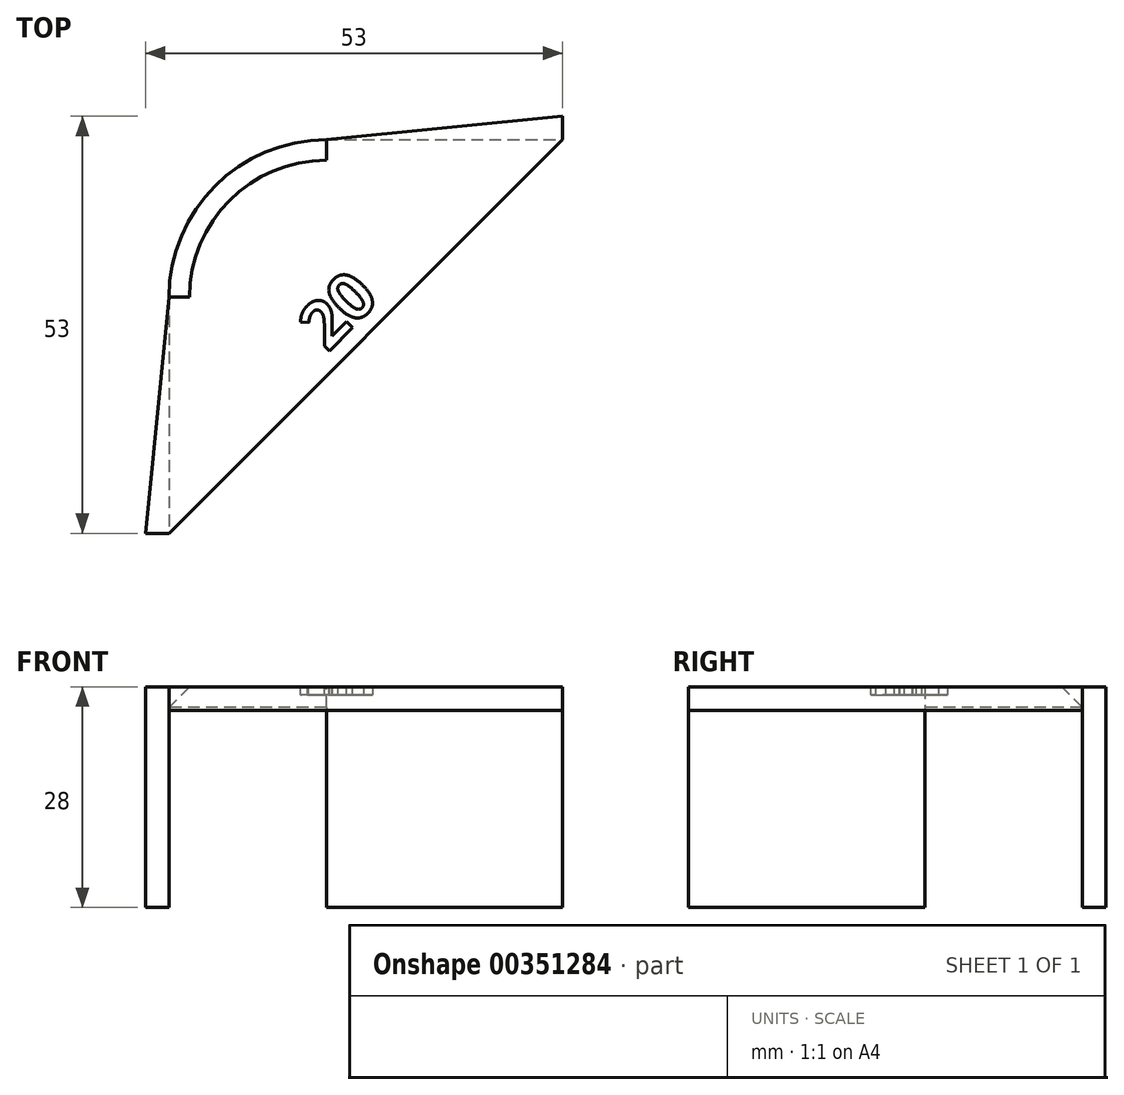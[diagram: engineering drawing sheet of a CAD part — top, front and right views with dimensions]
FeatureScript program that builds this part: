
annotation { "Feature Type Name" : "Feature", "Feature Type Description" : "" }
export const myFeature = defineFeature(function(context is Context, id is Id, definition is map)
    precondition{}
    {
        {
            var Q0;
            Q0=qCreatedBy(makeId("Top.planeOp"),FACE);
            var sketch = newSketch(context, id + "F0", { "sketchPlane" : qUnion([Q0])});
            skArc(sketch, "E0", {"start": v(0, 20) * mm, "mid": v(-14.14, 14.14) * mm, "end": v(-20, 0) * mm});
            skLineSegment(sketch, "E1", {"start": v(-20, 0) * mm, "end": v(-20, 20) * mm, "construction": true});
            skLineSegment(sketch, "E2", {"start": v(-20, 20) * mm, "end": v(0, 20) * mm, "construction": true});
            skPoint(sketch, "E3", {"position": v(0, 20) * mm});
            skPoint(sketch, "E4", {"position": v(-20, 0) * mm});
            skLineSegment(sketch, "E5", {"start": v(-20, 0) * mm, "end": v(-23, 0) * mm});
            skLineSegment(sketch, "E6", {"start": v(-23, -30) * mm, "end": v(-23, 0) * mm});
            skLineSegment(sketch, "E7", {"start": v(-23, -30) * mm, "end": v(-20, -30) * mm});
            skLineSegment(sketch, "E8", {"start": v(0, 20) * mm, "end": v(0, 23) * mm});
            skLineSegment(sketch, "E9", {"start": v(0, 23) * mm, "end": v(30, 23) * mm});
            skLineSegment(sketch, "E10", {"start": v(30, 23) * mm, "end": v(30, 20) * mm});
            skLineSegment(sketch, "E11", {"start": v(-20, -30) * mm, "end": v(30, 20) * mm});
            skPoint(sketch, "E12", {"position": v(-8.23, -18.23) * mm});
            skPoint(sketch, "E13", {"position": v(18.23, 8.23) * mm});
            skLineSegment(sketch, "E14", {"start": v(0, 20) * mm, "end": v(30, 20) * mm});
            skLineSegment(sketch, "E15", {"start": v(-20, 0) * mm, "end": v(-20, -30) * mm});
            skLineSegment(sketch, "E16", {"start": v(-20, -27.17) * mm, "end": v(27.17, 20) * mm, "construction": true});
            skPoint(sketch, "E17", {"position": v(3.59, -3.59) * mm});
            skLineSegment(sketch, "E18", {"start": v(0, 20) * mm, "end": v(30, 23) * mm});
            skLineSegment(sketch, "E19", {"start": v(-20, 0) * mm, "end": v(-23, -30) * mm});
            skLineSegment(sketch, "E20", {"start": v(0, 20) * mm, "end": v(0, 0) * mm});
            skLineSegment(sketch, "E21", {"start": v(0, 0) * mm, "end": v(-20, 0) * mm});
            skSolve(sketch);
        }
        {
            var Q0;
            Q0=makeQuery(id+"F0.imprint","IMPRINT",FACE,{"disambiguationData":[TD([[makeQuery(id+"F0.imprint","IMPRINT",EDGE,{"derivedFrom":sQuery(id+"F0.wireOp",EDGE,"E0")}),1.0]])]});
            extrude(context, id + "F1", {"entities" : qUnion([Q0]), "depth" : 3 * mm});
        }
        {
            var Q0;
            Q0=makeQuery(id+"F1.opExtrude","CAP_EDGE",EDGE,{"disambiguationData":[OSD([sQuery(id+"F0.wireOp",EDGE,"E0")])],"isStart":false});
            chamfer(context, id + "F2", {"entities" : qUnion([Q0]), "width" : 2.6 * mm, "tangentPropagation" : true});
        }
        {
            var Q0;
            Q0=makeQuery(id+"F0.imprint","IMPRINT",FACE,{"disambiguationData":[TD([[makeQuery(id+"F0.imprint","IMPRINT",EDGE,{"derivedFrom":sQuery(id+"F0.wireOp",EDGE,"E11")}),1.0]])]});
            var Q1;
            Q1=makeQuery(id+"F0.imprint","IMPRINT",FACE,{"disambiguationData":[TD([[makeQuery(id+"F0.imprint","IMPRINT",EDGE,{"derivedFrom":sQuery(id+"F0.wireOp",EDGE,"E10")}),-1.0]])]});
            var Q2;
            Q2=makeQuery(id+"F0.imprint","IMPRINT",FACE,{"disambiguationData":[TD([[makeQuery(id+"F0.imprint","IMPRINT",EDGE,{"derivedFrom":sQuery(id+"F0.wireOp",EDGE,"E7")}),1.0]])]});
            var Q3;
            Q3=makeQuery(id+"F1.opExtrude","CAP_FACE",FACE,{"disambiguationData":[OSD([sQuery(id+"F0.wireOp",EDGE,"E0"),sQuery(id+"F0.wireOp",EDGE,"E20"),sQuery(id+"F0.wireOp",EDGE,"E21")])],"isStart":false});
            extrude(context, id + "F3", {"entities" : qUnion([Q0, Q1, Q2]), "operationType" : NewBodyOperationType.ADD, "endBound" : BoundingType.UP_TO_SURFACE, "endBoundEntityFace" : qUnion([Q3]), "depth" : 3 * mm});
        }
        {
            var Q0;
            Q0=makeQuery(id+"F0.imprint","IMPRINT",FACE,{"disambiguationData":[TD([[makeQuery(id+"F0.imprint","IMPRINT",EDGE,{"derivedFrom":sQuery(id+"F0.wireOp",EDGE,"E10")}),-1.0]])]});
            var Q1;
            Q1=makeQuery(id+"F0.imprint","IMPRINT",FACE,{"disambiguationData":[TD([[makeQuery(id+"F0.imprint","IMPRINT",EDGE,{"derivedFrom":sQuery(id+"F0.wireOp",EDGE,"E7")}),1.0]])]});
            extrude(context, id + "F4", {"entities" : qUnion([Q0, Q1]), "operationType" : NewBodyOperationType.ADD, "oppositeDirection" : true, "depth" : 25 * mm});
        }
        {
            var Q0;
            Q0=makeQuery(id+"F3.opExtrude","CAP_FACE",FACE,{"disambiguationData":[OSD([sQuery(id+"F0.wireOp",EDGE,"E0"),sQuery(id+"F0.wireOp",EDGE,"E5"),sQuery(id+"F0.wireOp",EDGE,"E6"),sQuery(id+"F0.wireOp",EDGE,"E7"),sQuery(id+"F0.wireOp",EDGE,"E8"),sQuery(id+"F0.wireOp",EDGE,"E9"),sQuery(id+"F0.wireOp",EDGE,"E10"),sQuery(id+"F0.wireOp",EDGE,"E11")])],"isStart":false});
            var sketch = newSketch(context, id + "F5", { "sketchPlane" : qUnion([Q0])});
            skText(sketch, "E22", { "text": "20", "fontName": "OpenSans-Bold.ttf"});
            skPoint(sketch, "E23.0", {"position": v(3.59, -3.59) * mm});
            skLineSegment(sketch, "E24.0", {"start": v(-20, -27.17) * mm, "end": v(27.17, 20) * mm, "construction": true});
            const initialGuessF5  = {"E22": [0.00014, -0.00704, 0.7071, 0.7071, 0.006]};
            skSetInitialGuess(sketch, initialGuessF5);
            skSolve(sketch);
        }
        {
            var Q0;
            Q0 = qSketchRegion(id + "F5", true);
            extrude(context, id + "F6", {"entities" : qUnion([Q0]), "operationType" : NewBodyOperationType.REMOVE, "oppositeDirection" : true, "depth" : 1 * mm});
        }
    });
